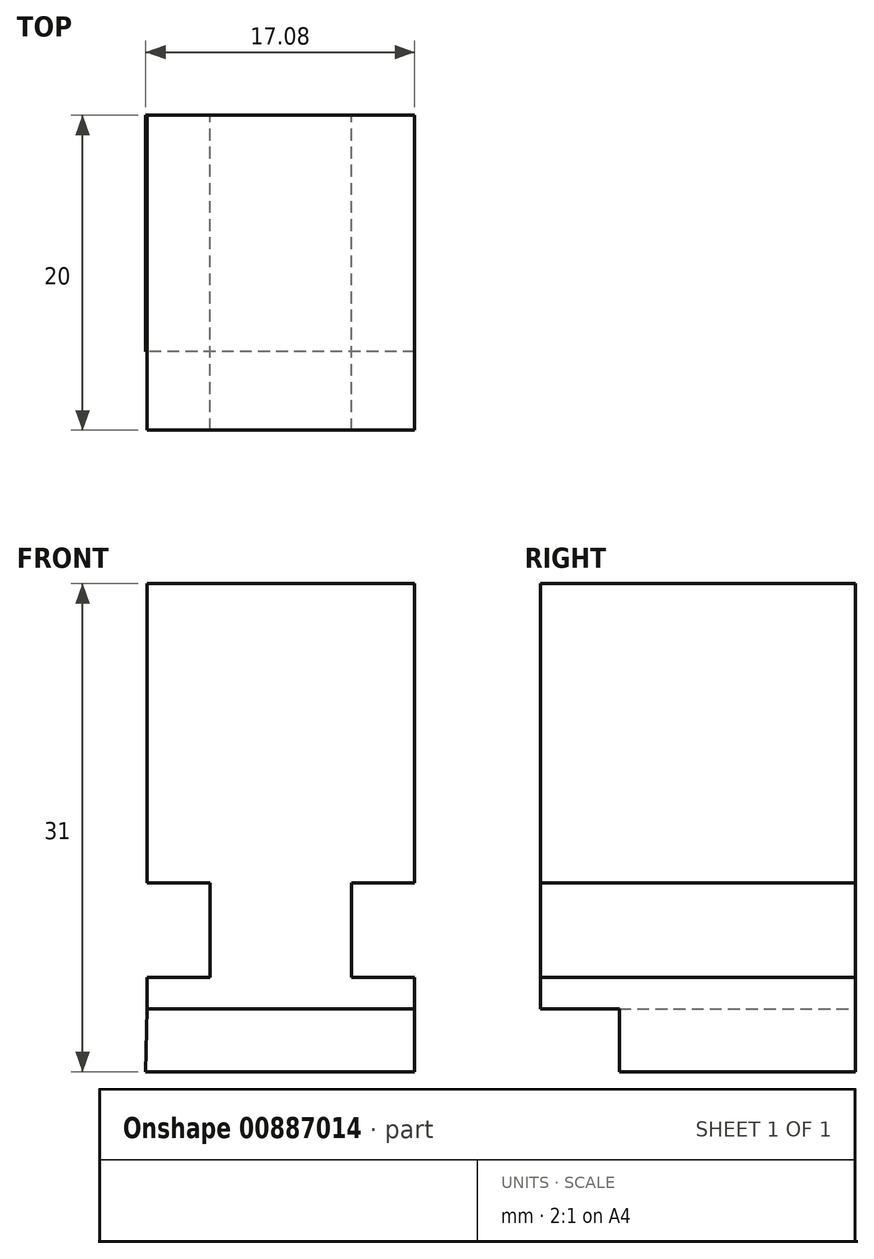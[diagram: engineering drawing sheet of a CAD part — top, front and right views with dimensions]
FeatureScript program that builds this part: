
annotation { "Feature Type Name" : "Feature", "Feature Type Description" : "" }
export const myFeature = defineFeature(function(context is Context, id is Id, definition is map)
    precondition{}
    {
        {
            var Q0;
            Q0=qCreatedBy(makeId("Front.planeOp"),FACE);
            var sketch = newSketch(context, id + "F0", { "sketchPlane" : qUnion([Q0])});
            skLineSegment(sketch, "E0", {"start": v(-83.14, -4.46) * mm, "end": v(-66.14, -4.46) * mm});
            skLineSegment(sketch, "E1", {"start": v(-66.14, -4.46) * mm, "end": v(-66.14, -23.46) * mm});
            skLineSegment(sketch, "E2", {"start": v(-66.14, -23.46) * mm, "end": v(-70.14, -23.46) * mm});
            skLineSegment(sketch, "E3", {"start": v(-70.14, -23.46) * mm, "end": v(-70.14, -29.46) * mm});
            skLineSegment(sketch, "E4", {"start": v(-70.14, -29.46) * mm, "end": v(-66.14, -29.46) * mm});
            skLineSegment(sketch, "E5", {"start": v(-66.14, -29.46) * mm, "end": v(-66.14, -31.46) * mm});
            skLineSegment(sketch, "E6", {"start": v(-66.14, -31.46) * mm, "end": v(-83.14, -31.46) * mm});
            skLineSegment(sketch, "E7", {"start": v(-83.14, -31.46) * mm, "end": v(-83.14, -29.46) * mm});
            skLineSegment(sketch, "E8", {"start": v(-83.14, -29.46) * mm, "end": v(-79.14, -29.46) * mm});
            skLineSegment(sketch, "E9", {"start": v(-79.14, -29.46) * mm, "end": v(-79.14, -23.46) * mm});
            skLineSegment(sketch, "E10", {"start": v(-79.14, -23.46) * mm, "end": v(-83.14, -23.46) * mm});
            skLineSegment(sketch, "E11", {"start": v(-83.14, -23.46) * mm, "end": v(-83.14, -4.46) * mm});
            skLineSegment(sketch, "E12", {"start": v(-66.14, -31.46) * mm, "end": v(-66.14, -35.46) * mm});
            skLineSegment(sketch, "E13", {"start": v(-66.14, -35.46) * mm, "end": v(-83.22, -35.46) * mm});
            skLineSegment(sketch, "E14", {"start": v(-83.22, -35.46) * mm, "end": v(-83.14, -31.46) * mm});
            skSolve(sketch);
        }
        {
            var Q0;
            Q0=makeQuery(id+"F0.imprint","IMPRINT",FACE,{"disambiguationData":[TD([[makeQuery(id+"F0.imprint","IMPRINT",EDGE,{"derivedFrom":sQuery(id+"F0.wireOp",EDGE,"E0")}),-1.0]])]});
            extrude(context, id + "F1", {"entities" : qUnion([Q0]), "depth" : 20 * mm, "offsetDistance" : 25 * mm});
        }
        {
            var Q0;
            Q0=makeQuery(id+"F0.imprint","IMPRINT",FACE,{"disambiguationData":[TD([[makeQuery(id+"F0.imprint","IMPRINT",EDGE,{"derivedFrom":sQuery(id+"F0.wireOp",EDGE,"E6")}),1.0]])]});
            extrude(context, id + "F2", {"entities" : qUnion([Q0]), "operationType" : NewBodyOperationType.ADD, "depth" : 15 * mm, "offsetDistance" : 25 * mm});
        }
    });
